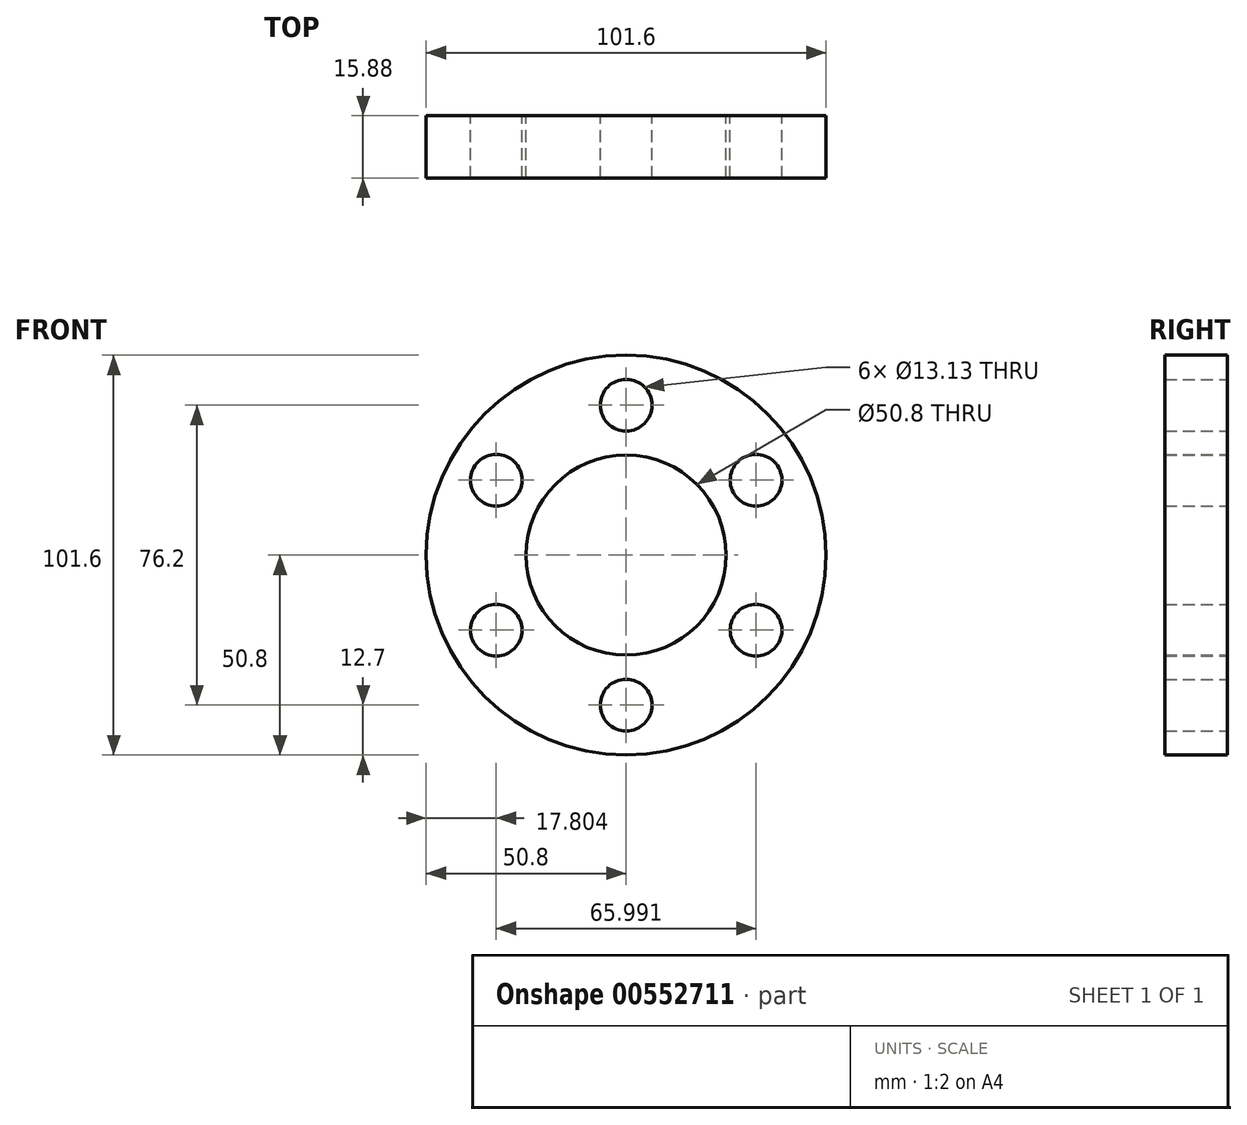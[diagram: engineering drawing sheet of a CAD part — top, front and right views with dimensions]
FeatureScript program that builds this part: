
annotation { "Feature Type Name" : "Feature", "Feature Type Description" : "" }
export const myFeature = defineFeature(function(context is Context, id is Id, definition is map)
    precondition{}
    {
        {
            var Q0;
            Q0=qCreatedBy(makeId("Front.planeOp"),FACE);
            var sketch = newSketch(context, id + "F0", { "sketchPlane" : qUnion([Q0])});
            skCircle(sketch, "E0", {"center": v(0, 0) * mm, "radius": 50.8 * mm});
            skCircle(sketch, "E1", {"center": v(0, 0) * mm, "radius": 25.4 * mm});
            skPoint(sketch, "E2", {"position": v(0, 38.1) * mm});
            skPoint(sketch, "E3.1.0", {"position": v(33, 19.05) * mm});
            skPoint(sketch, "E3.2.0", {"position": v(33, -19.05) * mm});
            skPoint(sketch, "E3.3.0", {"position": v(0, -38.1) * mm});
            skPoint(sketch, "E3.4.0", {"position": v(-33, -19.05) * mm});
            skPoint(sketch, "E3.5.0", {"position": v(-33, 19.05) * mm});
            skLineSegment(sketch, "E3.anchor1", {"start": v(0, 0) * mm, "end": v(0, 38.1) * mm, "construction": true});
            skLineSegment(sketch, "E3.anchor2", {"start": v(0, 0) * mm, "end": v(-33, 19.05) * mm, "construction": true});
            skCircle(sketch, "E4", {"center": v(0, 38.1) * mm, "radius": 6.57 * mm});
            skCircle(sketch, "E5.1.5", {"center": v(-33, 19.05) * mm, "radius": 6.57 * mm});
            skCircle(sketch, "E5.2.5", {"center": v(-33, -19.05) * mm, "radius": 6.57 * mm});
            skCircle(sketch, "E6.5.3.0", {"center": v(0, -38.1) * mm, "radius": 6.57 * mm});
            skCircle(sketch, "E6.5.4.0", {"center": v(33, -19.05) * mm, "radius": 6.57 * mm});
            skCircle(sketch, "E6.5.5.0", {"center": v(33, 19.05) * mm, "radius": 6.57 * mm});
            skSolve(sketch);
        }
        {
            var Q0;
            Q0=makeQuery(id+"F0.imprint","IMPRINT",FACE,{"disambiguationData":[TD([[makeQuery(id+"F0.imprint","IMPRINT",EDGE,{"derivedFrom":sQuery(id+"F0.wireOp",EDGE,"E0")}),1.0]])]});
            extrude(context, id + "F1", {"entities" : qUnion([Q0]), "endBound" : BoundingType.SYMMETRIC, "depth" : 15.88 * mm, "offsetDistance" : 25.4 * mm});
        }
    });
